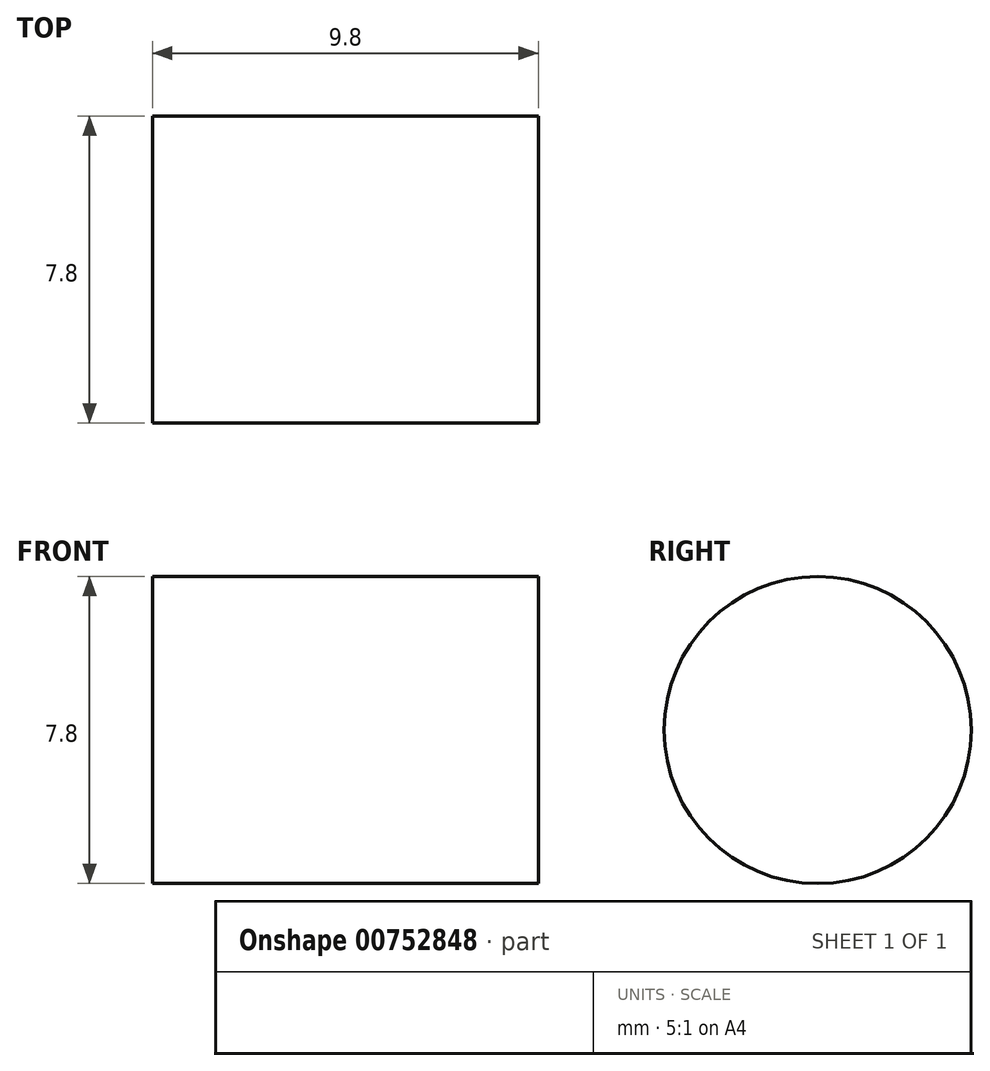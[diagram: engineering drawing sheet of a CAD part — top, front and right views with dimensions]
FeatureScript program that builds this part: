
annotation { "Feature Type Name" : "Feature", "Feature Type Description" : "" }
export const myFeature = defineFeature(function(context is Context, id is Id, definition is map)
    precondition{}
    {
        {
            var Q0;
            Q0=qCreatedBy(makeId("Right.planeOp"),FACE);
            var sketch = newSketch(context, id + "F0", { "sketchPlane" : qUnion([Q0])});
            skCircle(sketch, "E0", {"center": v(-34.11, 29.2) * mm, "radius": 3.9 * mm});
            skSolve(sketch);
        }
        {
            var Q0;
            Q0 = qSketchRegion(id + "F0", true);
            extrude(context, id + "F1", {"entities" : qUnion([Q0]), "depth" : 9.8 * mm, "offsetDistance" : 25 * mm});
        }
    });
